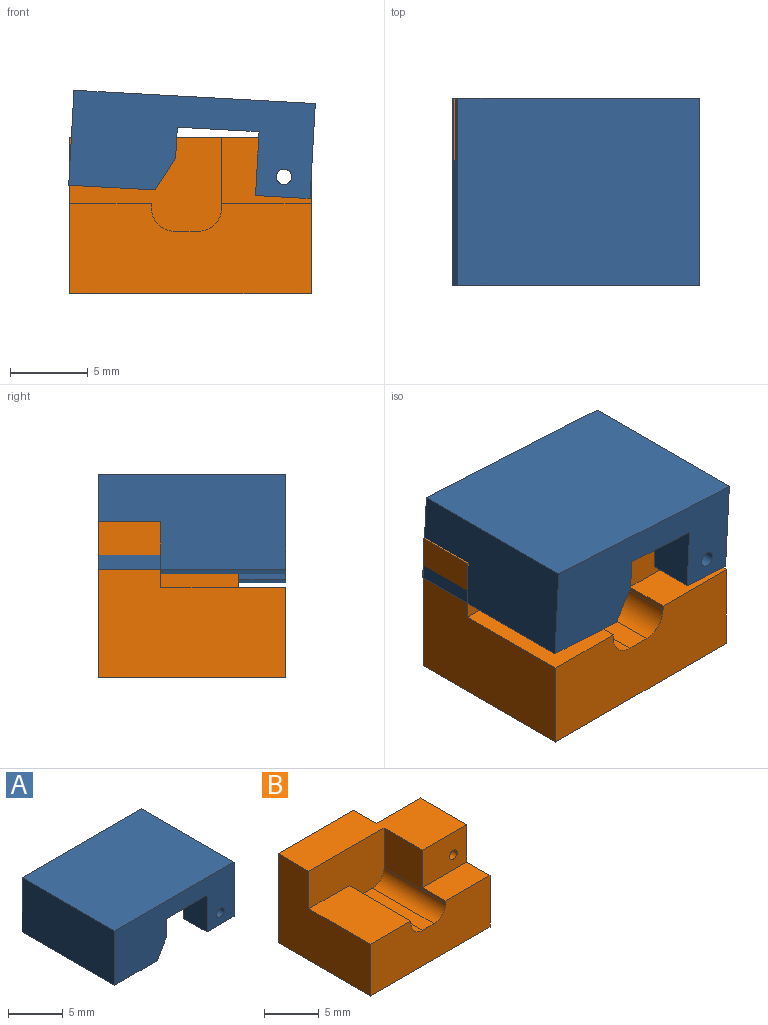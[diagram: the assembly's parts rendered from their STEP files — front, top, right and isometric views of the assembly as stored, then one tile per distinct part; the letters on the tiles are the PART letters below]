
ASSEMBLY  parts=2 mates=1
PART A: 17 faces, bbox 15.5x12x6.1 mm
  f0: plane 4.1x3mm, normal (-1,0,0), area 12.3mm2, adj f1,f12,f14,f16
  f1: plane 3.5x3mm, normal (0,0,-1), area 10.5mm2, adj f0,f2,f14,f16
  f2: plane 12x6.1mm, normal (1,0,0), area 48.6mm2, adj f1,f5,f6,f12,f13,f14,f15,f16
  f3: cylinder r=0.5mm len=3mm, axis (0,1,0), area 9.4mm2, adj f13,f15
  f4: plane 4.1x3mm, normal (-1,0,0), area 12.3mm2, adj f5,f12,f13,f15
  f5: plane 3.5x3mm, normal (0,0,-1), area 10.5mm2, adj f2,f4,f13,f15
  f6: plane 15.5x12mm, normal (0,0,1), area 186mm2, adj f2,f7,f13,f14
  f7: plane 12x6.1mm, normal (-1,0,0), area 73.2mm2, adj f6,f8,f13,f14
  f8: plane 12x5.56mm, normal (0,0,-1), area 66.7mm2, adj f7,f9,f13,f14
  f9: plane 12x2.07mm, normal (0.87,0,-0.5), area 28.7mm2, adj f8,f10,f13,f14
  f10: plane 12x2.03mm, normal (1,0,0), area 24.4mm2, adj f9,f12,f13,f14
  f11: cylinder r=0.5mm len=3mm, axis (0,1,0), area 9.4mm2, adj f14,f16
  f12: plane 12x8.75mm, normal (0,0,-1), area 84mm2, adj f0,f2,f4,f10,f13,f14,f15,f16
  f13: plane 15.5x6.1mm, normal (0,-1,0), area 71mm2, adj f2,f3,f4,f5,f6,f7,f8,f9
  f14: plane 15.5x6.1mm, normal (0,1,0), area 71mm2, adj f0,f1,f2,f6,f7,f8,f9,f10
  f15: plane 4.1x3.5mm, normal (0,1,0), area 13.6mm2, adj f2,f3,f4,f5,f12
  f16: plane 4.1x3.5mm, normal (0,-1,0), area 13.6mm2, adj f0,f1,f2,f11,f12
PART B: 19 faces, bbox 15.5x12x10 mm
  f0: cylinder r=0.5mm len=6mm, axis (0,-1,0), area 18.8mm2, adj f15,f16
  f1: plane 15.5x9mm, normal (0,0,1), area 73.5mm2, adj f3,f5,f6,f12,f13,f15,f16,f18
  f2: plane 15.5x5.8mm, normal (0,-1,0), area 82.8mm2, adj f3,f4,f5,f7,f8,f9,f10,f11
  f3: plane 12x10mm, normal (-1,0,0), area 86.4mm2, adj f1,f2,f4,f6,f7,f13
  f4: plane 15.5x12mm, normal (0,0,-1), area 186mm2, adj f2,f3,f5,f6
  f5: plane 12x10mm, normal (1,0,0), area 94.8mm2, adj f1,f2,f4,f6,f14,f15,f16,f17
  f6: plane 15.5x10mm, normal (0,1,0), area 130.9mm2, adj f1,f3,f4,f5,f17,f18
  f7: plane 8x5.25mm, normal (0,0,1), area 42mm2, adj f2,f3,f8,f13
  f8: plane 8x0.3mm, normal (1,0,0), area 2.4mm2, adj f2,f7,f9,f13
  f9: cylinder r=1.5mm len=8mm, axis (0,-1,0), area 18.8mm2, adj f2,f8,f10,f13
  f10: plane 8x1.5mm, normal (0,0,1), area 12mm2, adj f2,f9,f11,f13
  f11: cylinder r=1.5mm len=8mm, axis (0,-1,0), area 18.8mm2, adj f2,f10,f12,f13
  f12: plane 8x4.5mm, normal (-1,0,0), area 23.4mm2, adj f1,f2,f11,f13,f14,f15
  f13: plane 9.75x6mm, normal (0,-1,0), area 48.1mm2, adj f1,f3,f7,f8,f9,f10,f11,f12
  f14: plane 5.75x3mm, normal (0,0,1), area 17.2mm2, adj f2,f5,f12,f15
  f15: plane 5.75x4.2mm, normal (0,-1,0), area 23.4mm2, adj f0,f1,f5,f12,f14
  f16: plane 5.75x4.2mm, normal (0,1,0), area 23.4mm2, adj f0,f1,f5,f17,f18
  f17: plane 5.75x3mm, normal (0,0,1), area 17.2mm2, adj f5,f6,f16,f18
  f18: plane 4.2x3mm, normal (1,0,0), area 12.6mm2, adj f1,f6,f16,f17
PLACE A rot(axis=(0,1,0),3.2deg) t=(-1.49,2.63,-5.16)mm
PLACE B t=(-1.41,2.63,-5.49)mm fixed
MATE revolute B.f0 <-> A.f3  axis (0,-1,0) through (4.59,-2.37,-3.99)mm
